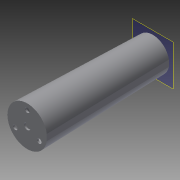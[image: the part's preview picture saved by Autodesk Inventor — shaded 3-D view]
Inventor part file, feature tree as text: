
AUTODESK INVENTOR PART (.ipt)
format: ipt  version: 2014 (Build 180170000, 170)  size: 237,056 bytes
history: native  units: mm
features: sketch x6, extrude x4, other x2, loft x1, shell x1, fillet x1, projected_geometry x1
ambient origin geometry x8: Origin, YZ Plane, XZ Plane, XY Plane, X Axis, Y Axis, Z Axis, Center Point
bodies: Body1 (feature_tree)
feature tree (16):
  other  "ソリッド1"
  sketch  "スケッチ1"
  other  "作業平面1"
  loft  "ロフト1"
  extrude  "押し出し1"  Depth=95.0mm
  shell  "シェル1"  Thickness=25.0mm
  extrude  "押し出し2"  TaperAngle=0.0deg  [1 undecoded]
  extrude  "押し出し4"  TaperAngle=0.0deg  [1 undecoded]
  extrude  "押し出し5"  Depth=3.5mm
  fillet  "フィレット2"  Radius=10.5mm
  sketch  "スケッチ2"
  sketch  "スケッチ3"
  sketch  "スケッチ4"
  sketch  "スケッチ6"
  projected_geometry  "投影ループ1"
  sketch  "スケッチ7"
note: 2 required parameter values undecoded (feature->parameter linkage not recoverable at this tier; creation-order binding heuristic only, values carry confidence <= 0.55)
